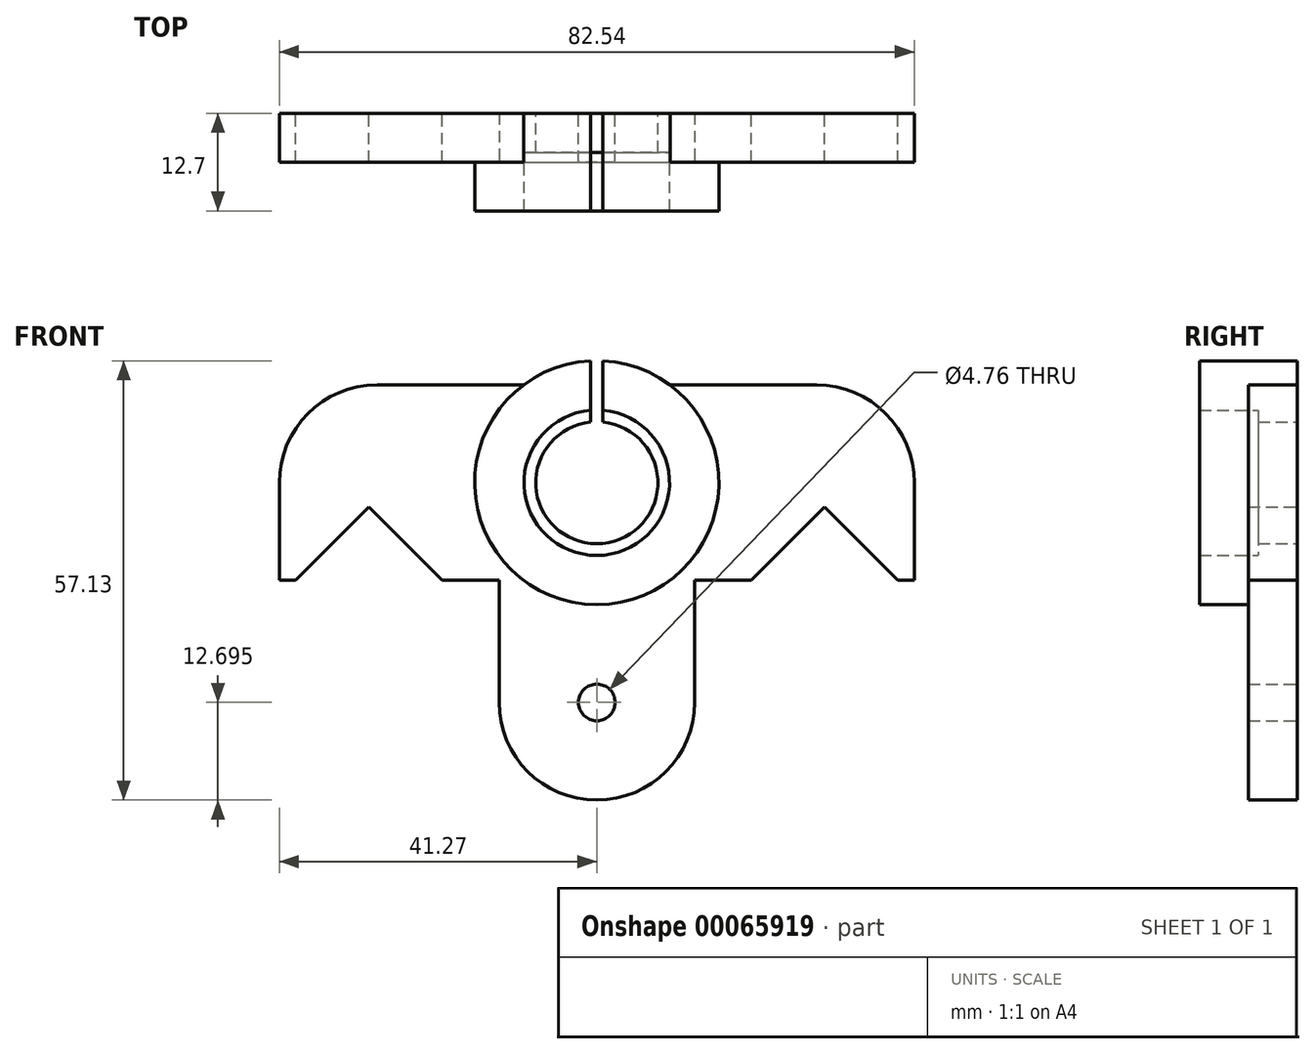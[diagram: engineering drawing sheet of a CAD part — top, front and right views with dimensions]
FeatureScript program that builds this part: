
annotation { "Feature Type Name" : "Feature", "Feature Type Description" : "" }
export const myFeature = defineFeature(function(context is Context, id is Id, definition is map)
    precondition{}
    {
        {
            var Q0;
            Q0=qCreatedBy(makeId("Front.planeOp"),FACE);
            var sketch = newSketch(context, id + "F0", { "sketchPlane" : qUnion([Q0])});
            skCircle(sketch, "E0", {"center": v(0, 0) * mm, "radius": 9.46 * mm});
            skCircle(sketch, "E1", {"center": v(0, 0) * mm, "radius": 15.88 * mm});
            skSolve(sketch);
        }
        {
            var Q0;
            Q0 = qSketchRegion(id + "F0", true);
            extrude(context, id + "F1", {"entities" : qUnion([Q0]), "depth" : 12.7 * mm});
        }
        {
            var Q0;
            Q0=qCreatedBy(makeId("Front.planeOp"),FACE);
            var sketch = newSketch(context, id + "F2", { "sketchPlane" : qUnion([Q0])});
            skLineSegment(sketch, "E2.bottom", {"start": v(-12.7, -9.53) * mm, "end": v(12.7, -9.52) * mm});
            skLineSegment(sketch, "E2.top", {"start": v(-12.7, -28.58) * mm, "end": v(12.7, -28.57) * mm});
            skLineSegment(sketch, "E2.left", {"start": v(-12.7, -9.52) * mm, "end": v(-12.7, -28.58) * mm});
            skLineSegment(sketch, "E2.right", {"start": v(12.7, -9.52) * mm, "end": v(12.7, -28.57) * mm});
            skArc(sketch, "E3", {"start": v(-12.7, -28.57) * mm, "mid": v(0, -41.28) * mm, "end": v(12.7, -28.57) * mm});
            skCircle(sketch, "E4", {"center": v(0, -28.57) * mm, "radius": 2.38 * mm});
            skSolve(sketch);
        }
        {
            var Q0;
            Q0 = qSketchRegion(id + "F2", true);
            extrude(context, id + "F3", {"entities" : qUnion([Q0]), "operationType" : NewBodyOperationType.ADD, "depth" : 6.35 * mm});
        }
        {
            var Q0;
            Q0=qCreatedBy(makeId("Front.planeOp"),FACE);
            var sketch = newSketch(context, id + "F4", { "sketchPlane" : qUnion([Q0])});
            skLineSegment(sketch, "E5.bottom", {"start": v(9.52, 12.7) * mm, "end": v(41.28, 12.7) * mm});
            skLineSegment(sketch, "E5.top", {"start": v(9.52, -12.7) * mm, "end": v(41.28, -12.7) * mm});
            skLineSegment(sketch, "E5.left", {"start": v(9.52, 12.7) * mm, "end": v(9.52, -12.7) * mm});
            skLineSegment(sketch, "E5.right", {"start": v(41.28, 12.7) * mm, "end": v(41.28, -12.7) * mm});
            skLineSegment(sketch, "E6", {"start": v(39.14, -12.7) * mm, "end": v(29.61, -3.18) * mm});
            skLineSegment(sketch, "E7", {"start": v(29.61, -3.18) * mm, "end": v(20.09, -12.7) * mm});
            skSolve(sketch);
        }
        {
            var Q0;
            Q0=makeQuery(id+"F4.imprint","IMPRINT",FACE,{"disambiguationData":[TD([[makeQuery(id+"F4.imprint","IMPRINT",EDGE,{"derivedFrom":sQuery(id+"F4.wireOp",EDGE,"E5.bottom")}),-1.0]])]});
            extrude(context, id + "F5", {"entities" : qUnion([Q0]), "depth" : 6.35 * mm});
        }
        {
            var Q0;
            Q0=makeQuery(id+"F5.opExtrude","SWEPT_BODY",BODY,{"disambiguationData":[OSD([sQuery(id+"F4.wireOp",EDGE,"E5.bottom"),sQuery(id+"F4.wireOp",EDGE,"E5.top"),sQuery(id+"F4.wireOp",EDGE,"E5.left"),sQuery(id+"F4.wireOp",EDGE,"E5.right"),sQuery(id+"F4.wireOp",EDGE,"E6"),sQuery(id+"F4.wireOp",EDGE,"E7")])]});
            var Q1;
            Q1=qCreatedBy(makeId("Right.planeOp"),FACE);
            mirror(context, id + "F6", {"operationType" : NewBodyOperationType.ADD, "entities" : qUnion([Q0]), "mirrorPlane" : qUnion([Q1])});
        }
        {
            var Q0;
            Q0=makeQuery(id+"F5.opExtrude","SWEPT_EDGE",EDGE,{"disambiguationData":[OSD([sQuery(id+"F4.wireOp",EDGE,"E5.bottom"),sQuery(id+"F4.wireOp",EDGE,"E5.right")])]});
            var Q1;
            Q1=makeQuery(id+"F6.opPattern","COPY",EDGE,{"derivedFrom":makeQuery(id+"F5.opExtrude","SWEPT_EDGE",EDGE,{"disambiguationData":[OSD([sQuery(id+"F4.wireOp",EDGE,"E5.bottom"),sQuery(id+"F4.wireOp",EDGE,"E5.right")])]}),"instanceName":"1"});
            fillet(context, id + "F7", {"entities" : qUnion([Q0, Q1]), "radius" : 12.7 * mm, "tangentPropagation" : true, "allowEdgeOverflow" : false});
        }
        {
            var Q0;
            Q0=qCreatedBy(makeId("Front.planeOp"),FACE);
            var sketch = newSketch(context, id + "F8", { "sketchPlane" : qUnion([Q0])});
            skLineSegment(sketch, "E8.bottom", {"start": v(-0.8, 18.6) * mm, "end": v(0.8, 18.6) * mm});
            skLineSegment(sketch, "E8.top", {"start": v(-0.8, 0.58) * mm, "end": v(0.8, 0.58) * mm});
            skLineSegment(sketch, "E8.left", {"start": v(-0.8, 18.6) * mm, "end": v(-0.8, 0.58) * mm});
            skLineSegment(sketch, "E8.right", {"start": v(0.8, 18.6) * mm, "end": v(0.8, 0.58) * mm});
            skLineSegment(sketch, "E9", {"start": v(0, 0) * mm, "end": v(0, 0.58) * mm, "construction": true});
            skSolve(sketch);
        }
        {
            var Q0;
            Q0 = qSketchRegion(id + "F8", true);
            extrude(context, id + "F9", {"entities" : qUnion([Q0]), "operationType" : NewBodyOperationType.REMOVE, "endBound" : BoundingType.THROUGH_ALL, "depth" : 25.4 * mm});
        }
        {
            var Q0;
            Q0=qCreatedBy(makeId("Front.planeOp"),FACE);
            var sketch = newSketch(context, id + "F10", { "sketchPlane" : qUnion([Q0])});
            skArc(sketch, "E10", {"start": v(-0.8, 9.43) * mm, "mid": v(0, -9.46) * mm, "end": v(0.8, 9.43) * mm});
            skArc(sketch, "E11", {"start": v(-0.8, 7.9) * mm, "mid": v(0, -7.94) * mm, "end": v(0.8, 7.9) * mm});
            skLineSegment(sketch, "E12", {"start": v(0.8, 9.43) * mm, "end": v(0.8, 7.9) * mm});
            skLineSegment(sketch, "E13", {"start": v(-0.8, 7.9) * mm, "end": v(-0.8, 9.43) * mm});
            skSolve(sketch);
        }
        {
            var Q0;
            Q0 = qSketchRegion(id + "F10", true);
            extrude(context, id + "F11", {"entities" : qUnion([Q0]), "operationType" : NewBodyOperationType.ADD, "depth" : 5.08 * mm});
        }
    });
